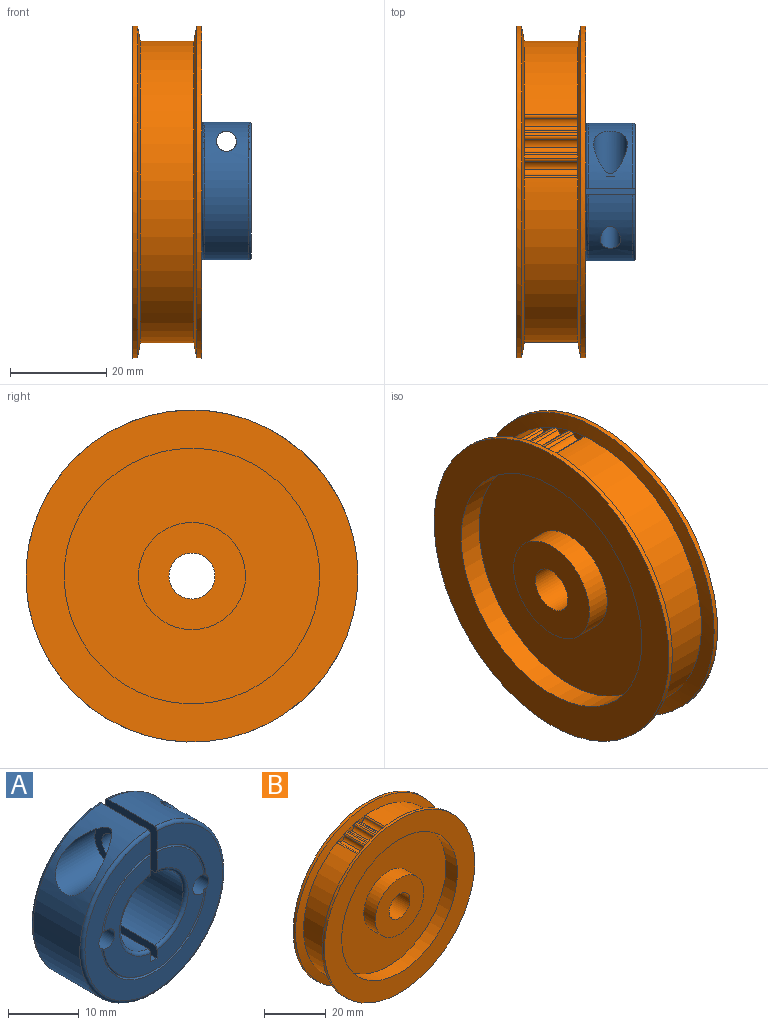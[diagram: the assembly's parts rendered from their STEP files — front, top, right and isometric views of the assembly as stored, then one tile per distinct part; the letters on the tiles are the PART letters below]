
ASSEMBLY  parts=2 mates=1
PART A: 26 faces, bbox 30.9x10.5x30.9 mm
  f0: torus R=10.32mm, axis (0,1,0), area 8.5mm2, adj f4,f5,f11,f25
  f1: torus R=10.32mm, axis (0,1,0), area 8.5mm2, adj f2,f5,f11,f24
  f2: plane 10.34x7.97mm, normal (1,0,0), area 68.2mm2, adj f1,f3,f5,f9,f11,f12,f15,f16
  f3: cylinder r=14.29mm len=28.58mm, axis (0,1,0), area 741mm2, adj f2,f4,f15,f16,f20,f21
  f4: plane 10.34x7.97mm, normal (-1,0,0), area 68.2mm2, adj f0,f3,f5,f10,f11,f12,f13,f14
  f5: plane 27.54x27.53mm, normal (0,-1,0), area 243.1mm2, adj f0,f1,f2,f4,f15,f19,f24,f25
  f6: plane 10.34x2.04mm, normal (-1,0,0), area 20.7mm2, adj f7,f10,f11,f12,f13,f14
  f7: plane 10.32x1.27mm, normal (0,0,1), area 13.1mm2, adj f6,f8,f11,f12
  f8: plane 10.34x2.04mm, normal (1,0,0), area 20.7mm2, adj f7,f9,f11,f12,f17,f18
  f9: cylinder r=6.35mm len=12.64mm, axis (0,1,0), area 173.5mm2, adj f2,f8,f17,f18
  f10: cylinder r=6.35mm len=12.64mm, axis (0,1,0), area 173.5mm2, adj f4,f6,f13,f14
  f11: plane 20.24x20.05mm, normal (0,-1,0), area 155.9mm2, adj f0,f1,f2,f4,f6,f7,f8,f13
  f12: plane 27.54x27.53mm, normal (0,1,0), area 421.2mm2, adj f2,f4,f6,f7,f8,f14,f16,f18
  f13: torus R=6.87mm, axis (0,-1,0), area 15.6mm2, adj f4,f6,f10,f11
  f14: torus R=6.87mm, axis (0,-1,0), area 15.6mm2, adj f4,f6,f10,f12
  f15: torus R=13.77mm, axis (0,-1,0), area 70.8mm2, adj f2,f3,f4,f5
  f16: torus R=13.77mm, axis (0,-1,0), area 70.8mm2, adj f2,f3,f4,f12
  f17: torus R=6.87mm, axis (0,-1,0), area 15.6mm2, adj f2,f8,f9,f11
  f18: torus R=6.87mm, axis (0,-1,0), area 15.6mm2, adj f2,f8,f9,f12
  f19: torus R=10.32mm, axis (0,1,0), area 17.8mm2, adj f5,f11,f24,f25
  f20: cylinder r=2.08mm len=11.06mm, axis (1,0,0), area 118.2mm2, adj f3,f4
  f21: cylinder r=3.49mm len=9.44mm, axis (1,0,0), area 131.4mm2, adj f3,f23
  f22: cylinder r=2.08mm len=4.17mm, axis (1,0,0), area 32.6mm2, adj f2,f23
  f23: plane 6.99x6.99mm, normal (-1,0,0), area 24.7mm2, adj f21,f22
  f24: cylinder r=1.59mm len=10.32mm, axis (0,1,0), area 102.8mm2, adj f1,f5,f11,f12,f19
  f25: cylinder r=1.59mm len=10.32mm, axis (0,1,0), area 102.8mm2, adj f0,f5,f11,f12,f19
PART B: 36 faces, bbox 68.8x14.3x68.8 mm
  f0: revolved ~22.23x22.23mm, area 365.8mm2, adj f23,f35
  f1: revolved ~14.29x9.54mm, area 856.2mm2, adj f3,f35
  f2: plane 68.83x68.83mm, normal (0,1,0), area 1516.4mm2, adj f5,f32
  f3: plane 22.23x22.23mm, normal (0,1,0), area 316.5mm2, adj f1,f34
  f4: revolved ~68.83x68.83mm, area 445.4mm2, adj f6,f21
  f5: revolved ~68.83x68.83mm, area 222.7mm2, adj f2,f16
  f6: revolved ~68.83x68.83mm, area 662.5mm2, adj f4,f7,f9,f10,f11,f13,f26
  f7: plane 3.62x2.45mm, normal (0,1,0), area 3.9mm2, adj f6,f8,f18,f19,f20
  f8: revolved ~11.11x0.74mm, area 8.9mm2, adj f7,f10,f17,f20
  f9: revolved ~11.11x0.82mm, area 9.3mm2, adj f6,f12,f16,f27
  f10: revolved ~62.45x62.34mm, area 2027.9mm2, adj f6,f8,f16,f25
  f11: revolved ~11.11x0.78mm, area 9.3mm2, adj f6,f14,f16,f18
  f12: revolved ~11.11x0.59mm, area 8.9mm2, adj f9,f13,f15,f30
  f13: plane 3.87x2.18mm, normal (0,1,0), area 3.9mm2, adj f6,f12,f14,f30,f31
  f14: revolved ~11.11x0.71mm, area 8.9mm2, adj f11,f13,f15,f31
  f15: plane 3.87x2.18mm, normal (0,-1,0), area 3.9mm2, adj f12,f14,f16,f30,f31
  f16: revolved ~68.83x68.83mm, area 1325mm2, adj f5,f9,f10,f11,f15,f17,f24
  f17: plane 3.62x2.45mm, normal (0,-1,0), area 3.9mm2, adj f8,f16,f18,f19,f20
  f18: revolved ~11.11x0.65mm, area 8.9mm2, adj f7,f11,f17,f19
  f19: revolved ~11.11x1.7mm, area 21.7mm2, adj f7,f17,f18,f20
  f20: revolved ~11.11x1.8mm, area 21.7mm2, adj f7,f8,f17,f19
  f21: plane 68.83x68.83mm, normal (0,-1,0), area 1516.4mm2, adj f4,f22
  f22: revolved ~52.98x52.98mm, area 872mm2, adj f21,f23
  f23: plane 52.98x52.98mm, normal (0,-1,0), area 1816.9mm2, adj f0,f22
  f24: plane 4.02x1.9mm, normal (0,-1,0), area 3.9mm2, adj f16,f25,f27,f28,f29
  f25: revolved ~11.11x0.54mm, area 8.9mm2, adj f10,f24,f26,f29
  f26: plane 4.02x1.9mm, normal (0,1,0), area 3.9mm2, adj f6,f25,f27,f28,f29
  f27: revolved ~11.11x0.67mm, area 8.9mm2, adj f9,f24,f26,f28
  f28: revolved ~11.11x1.59mm, area 21.7mm2, adj f24,f26,f27,f29
  f29: revolved ~11.11x1.39mm, area 21.7mm2, adj f24,f25,f26,f28
  f30: revolved ~11.11x1.56mm, area 21.7mm2, adj f12,f13,f15,f31
  f31: revolved ~11.11x1.72mm, area 21.7mm2, adj f13,f14,f15,f30
  f32: revolved ~52.98x52.98mm, area 889.6mm2, adj f2,f33
  f33: plane 52.98x52.98mm, normal (0,1,0), area 1816.9mm2, adj f32,f34
  f34: revolved ~22.23x22.23mm, area 373.2mm2, adj f3,f33
  f35: plane 22.23x22.23mm, normal (0,-1,0), area 316.5mm2, adj f0,f1
PLACE A rot(axis=(0,0,-1),90deg) t=(9.43,9.13,22.3)mm
PLACE B rot(axis=(0,0,-1),90deg) t=(-2.87,9.13,22.1)mm
MATE fastened A.f11 <-> B.f3  axis (-1,0,0) through (4.28,9.13,22.1)mm
